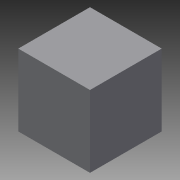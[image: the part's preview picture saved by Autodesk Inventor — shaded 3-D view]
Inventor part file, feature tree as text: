
AUTODESK INVENTOR PART (.ipt)
format: ipt  version: 2014 (Build 180170000, 170)  size: 68,096 bytes
history: native  units: in
note: dims shown in document units (in); Inventor stores cm internally (conversion verified against a paired STEP export)
features: extrude x1, sketch x1
ambient origin geometry x8: Origin, YZ Plane, XZ Plane, XY Plane, X Axis, Y Axis, Z Axis, Center Point
bodies: Solid1 (feature_tree)
feature tree (2):
  extrude  "Extrusion1"  Depth=1.0in
  sketch  "Sketch1"  dims[d0=1.0in d1=1.0in d2=1.0in d3=0.0in]
